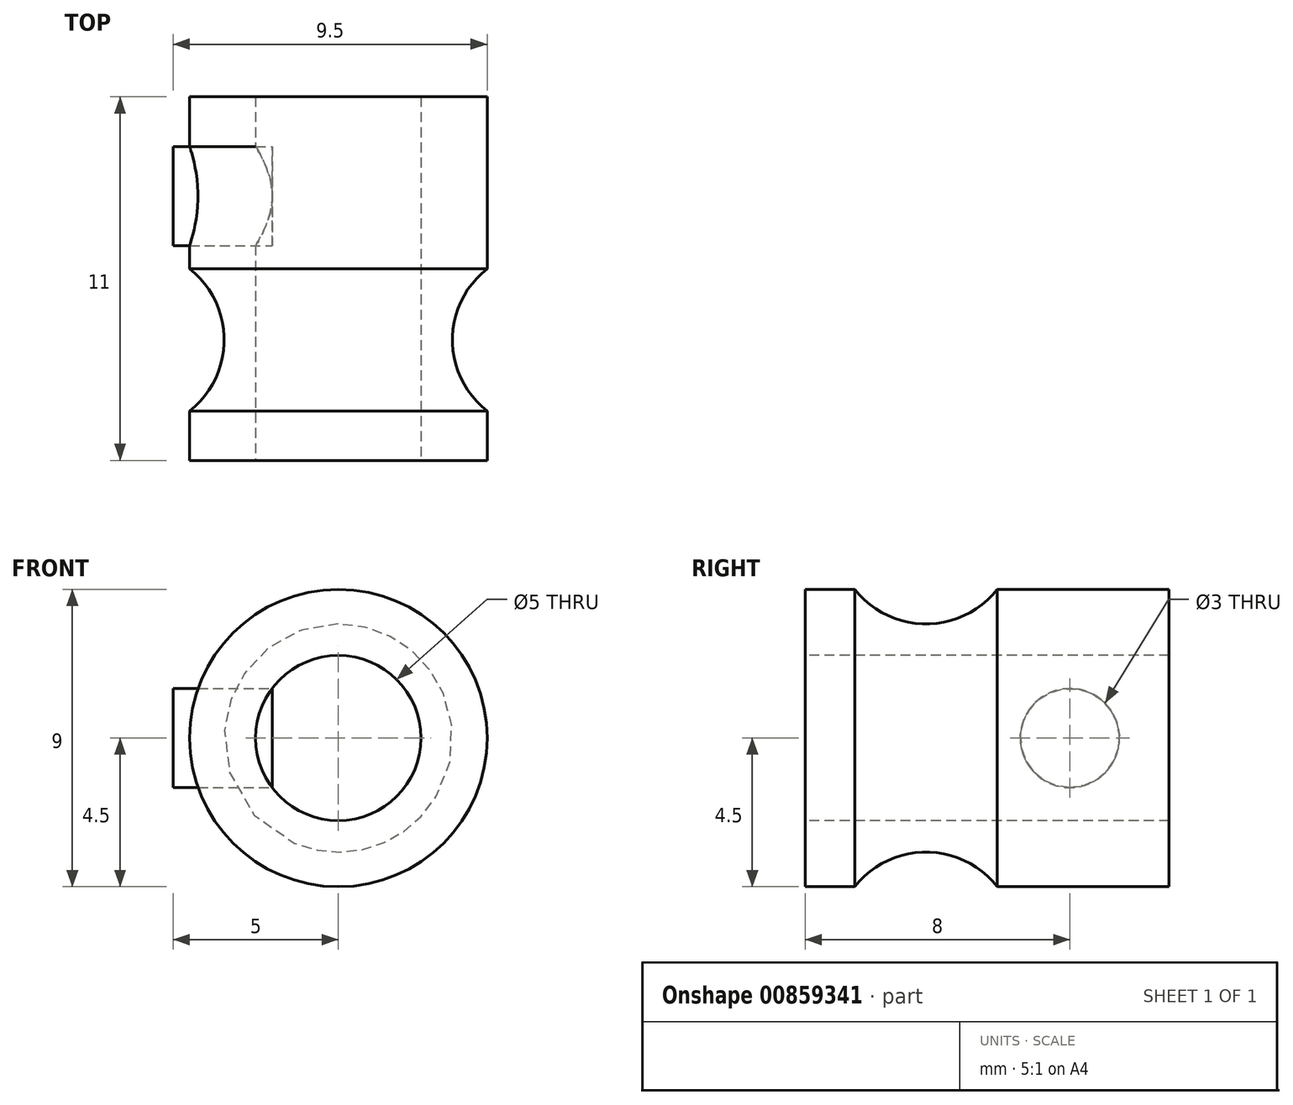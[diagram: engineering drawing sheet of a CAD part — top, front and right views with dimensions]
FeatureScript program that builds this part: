
annotation { "Feature Type Name" : "Feature", "Feature Type Description" : "" }
export const myFeature = defineFeature(function(context is Context, id is Id, definition is map)
    precondition{}
    {
        {
            var Q0;
            Q0=qCreatedBy(makeId("Front.planeOp"),FACE);
            var sketch = newSketch(context, id + "F0", { "sketchPlane" : qUnion([Q0])});
            skCircle(sketch, "E0", {"center": v(0, 0) * mm, "radius": 4.5 * mm});
            skSolve(sketch);
        }
        {
            var Q0;
            Q0=makeQuery(id+"F0.imprint","IMPRINT",FACE,{"disambiguationData":[TD([[makeQuery(id+"F0.imprint","IMPRINT",EDGE,{"derivedFrom":sQuery(id+"F0.wireOp",EDGE,"E0")}),1.0]])]});
            extrude(context, id + "F1", {"entities" : qUnion([Q0]), "depth" : 11 * mm, "offsetDistance" : 25 * mm});
        }
        {
            var Q0;
            Q0=makeQuery(id+"F1.opExtrude","CAP_FACE",FACE,{"disambiguationData":[OSD([sQuery(id+"F0.wireOp",EDGE,"E0")])],"isStart":false});
            var sketch = newSketch(context, id + "F2", { "sketchPlane" : qUnion([Q0])});
            skCircle(sketch, "E1", {"center": v(0, 0) * mm, "radius": 2.5 * mm});
            skSolve(sketch);
        }
        {
            var Q0;
            Q0=makeQuery(id+"F2.imprint","IMPRINT",FACE,{"disambiguationData":[TD([[makeQuery(id+"F2.imprint","IMPRINT",EDGE,{"derivedFrom":sQuery(id+"F2.wireOp",EDGE,"E1")}),1.0]])]});
            extrude(context, id + "F3", {"entities" : qUnion([Q0]), "operationType" : NewBodyOperationType.REMOVE, "endBound" : BoundingType.THROUGH_ALL, "oppositeDirection" : true, "depth" : 25 * mm, "offsetDistance" : 25 * mm});
        }
        {
            var Q0;
            Q0=qCreatedBy(makeId("Right.planeOp"),FACE);
            var sketch = newSketch(context, id + "F4", { "sketchPlane" : qUnion([Q0])});
            skArc(sketch, "E2", {"start": v(-9.5, 4.5) * mm, "mid": v(-7.35, 3.45) * mm, "end": v(-5.2, 4.5) * mm});
            skLineSegment(sketch, "E3", {"start": v(-5.2, 4.5) * mm, "end": v(-9.5, 4.5) * mm});
            skLineSegment(sketch, "E4", {"start": v(-11, 4.5) * mm, "end": v(0, 4.5) * mm});
            skLineSegment(sketch, "E5", {"start": v(0, 0) * mm, "end": v(-16.05, 0) * mm, "construction": true});
            skSolve(sketch);
        }
        {
            var Q0;
            Q0=makeQuery(id+"F4.imprint","IMPRINT",FACE,{"disambiguationData":[TD([[makeQuery(id+"F4.imprint","IMPRINT",EDGE,{"derivedFrom":sQuery(id+"F4.wireOp",EDGE,"E2")}),1.0]])]});
            var Q1;
            Q1=sQuery(id+"F4.wireOp",EDGE,"E5");
            revolve(context, id + "F5", {"operationType" : NewBodyOperationType.REMOVE, "surfaceOperationType" : NewSurfaceOperationType.NEW, "entities" : qUnion([Q0]), "axis" : qUnion([Q1]), "revolveType" : RevolveType.FULL});
        }
        {
            var Q0;
            Q0=qCreatedBy(makeId("Right.planeOp"),FACE);
            var sketch = newSketch(context, id + "F6", { "sketchPlane" : qUnion([Q0])});
            skPoint(sketch, "E6", {"position": v(-3, 0) * mm});
            skCircle(sketch, "E7", {"center": v(-3, 0) * mm, "radius": 1.5 * mm});
            skSolve(sketch);
        }
        {
            var Q0;
            Q0 = qSketchRegion(id + "F6", true);
            extrude(context, id + "F7", {"entities" : qUnion([Q0]), "operationType" : NewBodyOperationType.REMOVE, "endBound" : BoundingType.THROUGH_ALL, "oppositeDirection" : true, "depth" : 25 * mm, "offsetDistance" : 25 * mm});
        }
        {
            var Q0;
            Q0 = qSketchRegion(id + "F6", true);
            extrude(context, id + "F8", {"entities" : qUnion([Q0]), "depth" : -5 * mm, "offsetDistance" : 25 * mm, "hasSecondDirection" : true, "secondDirectionOppositeDirection" : true, "secondDirectionDepth" : 2 * mm});
        }
    });
